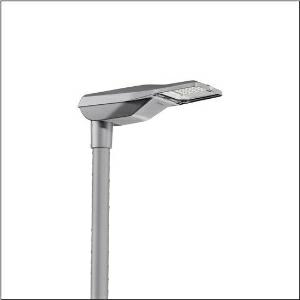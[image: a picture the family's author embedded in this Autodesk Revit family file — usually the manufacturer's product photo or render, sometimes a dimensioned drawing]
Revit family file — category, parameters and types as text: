
# Revit family: streetlight_sl_21_iq_micro___st0_8a_5xe1c31g08db_5951
name_source: partatom
category: Lighting Fixtures
units: mm (PartAtom-declared; Revit-internal decimal feet)

## family parameters
Cut with Voids When Loaded = No
Host = Face
Light Source = No
Part Type = Normal
Room Calculation Point = No
Round Connector Dimension = Use Diameter
Shared = No

## types (1)
- --- (1 x LED, 4810 lm, 36.4 W, 3000K)
    Apparent Load = 36 VA
    CIE Flux Codes = 38 75 97 100 100
    Color Rendering = 70
    Color Temperature = 3000K
    Default Elevation = 1800 mm
    Description = Streetlight SL 21 iQ micro, mast luminaire, primary light control with lens, of PMMA, primary optical cover: cover, of toughened safety glass, transparent, light distribution: ST0.8a, light emission: direct distribution, primary light characteristic: asymmetric, installation type: post-top, side-entry, LED, High Power LED, rated luminous flux: 4.810lm, luminous efficacy: 132lm/W, light colour: 730, colour temperature: 3000K, control gear: iQ Street-Remote, control: Street-Remote, Auto-Match, Temp-Guard, Lumen-Switch, Night-Set, Smart-Wire, Light-Fading, Desk-Remote (wireless, voltage-free reading and setting of iQ features in the workshop via application-optimized NFC function/RFID function), optimised constant luminous flux control (CLO 2.0), pre-setting: linear dimming characteristic, mains connection: 220..240V, AC, 50/60Hz, start of lifetime: 36W, end of service life: 38W, reduction: 16W, luminaire housing, of diecast aluminium, powder-coated, Siteco® metallic grey (DB 702S), corrosivity category C5 mid according to DIN EN ISO 12944, please order mast flange separately, inclination adjustable: 0°, 5°, 10°, 15°, sealing non-destructively replaceable, multi-level sealing system, length: 528mm, width: 235mm, height: 110mm, mast flange for spigot size: 42mm (side-entry): 5XC10008XM4, 60/48mm (side-entry/post-top): 5XC10108XM2, 76/60mm (side-entry/post-top): 5XC10108XM1, protection rating (complete): IP66, insulation class (complete): insulation class II (safety insulation), certification: CE, ENEC, ENEC+, VDE, impact resistance: IK10, permissible operating ambient temperature for outdoor applications: -40..+50°C, standard-compliant lighting for roads and squares, packaging unit: 1 piece

Light Distribution: ST0.8a
    Height = 110 mm
    Lamp = 1 x LED
    Lamp Light Flux = 4810 lm
    Lamp Power = 36.4 W
    Lamp count = 1
    Length = 528 mm
    Luminous efficacy = 132 lm/W
    Manufacturer = Siteco
    ModVariant = No
    Model = 5XE1C31G08DB
    Number of Poles = 1
    OnlyDefault = Yes
    Power Factor = 1
    Product Name = Streetlight SL 21 iQ micro | ST0.8a
    Product group = mast luminaire | pylon top
    ProductGroupID = 6100
    Protection Class = Protection class II
    Protection Degree = IP 66
    RLX_Detail_Level = 1
    RLX_Emergency_Light_Flux = 0 lm
    RLX_Emergency_Type = 0
    RLX_Emergency_Type_DB = No
    RlxData = <blob elided: 99313 chars, md5=6d6488e6>
    Socket = socket
    Standby Power = 0 W
    System Light Flux = 4810 lm
    System Power = 36 W
    Type Comments = factory setting: luminous flux: 100 % | dim-lin: 254 | 715 mA
    Type Image = l_1006881.jpg
    URL = http://relux.com
    VarID = @adj_154580
    Voltage = 0 V
    Weight = 0.00 kg
    Width = 235 mm

## geometry (parser evidence)
native form markers: Blend x4, Sweep x9
no freeform markers — native parametric forms only
